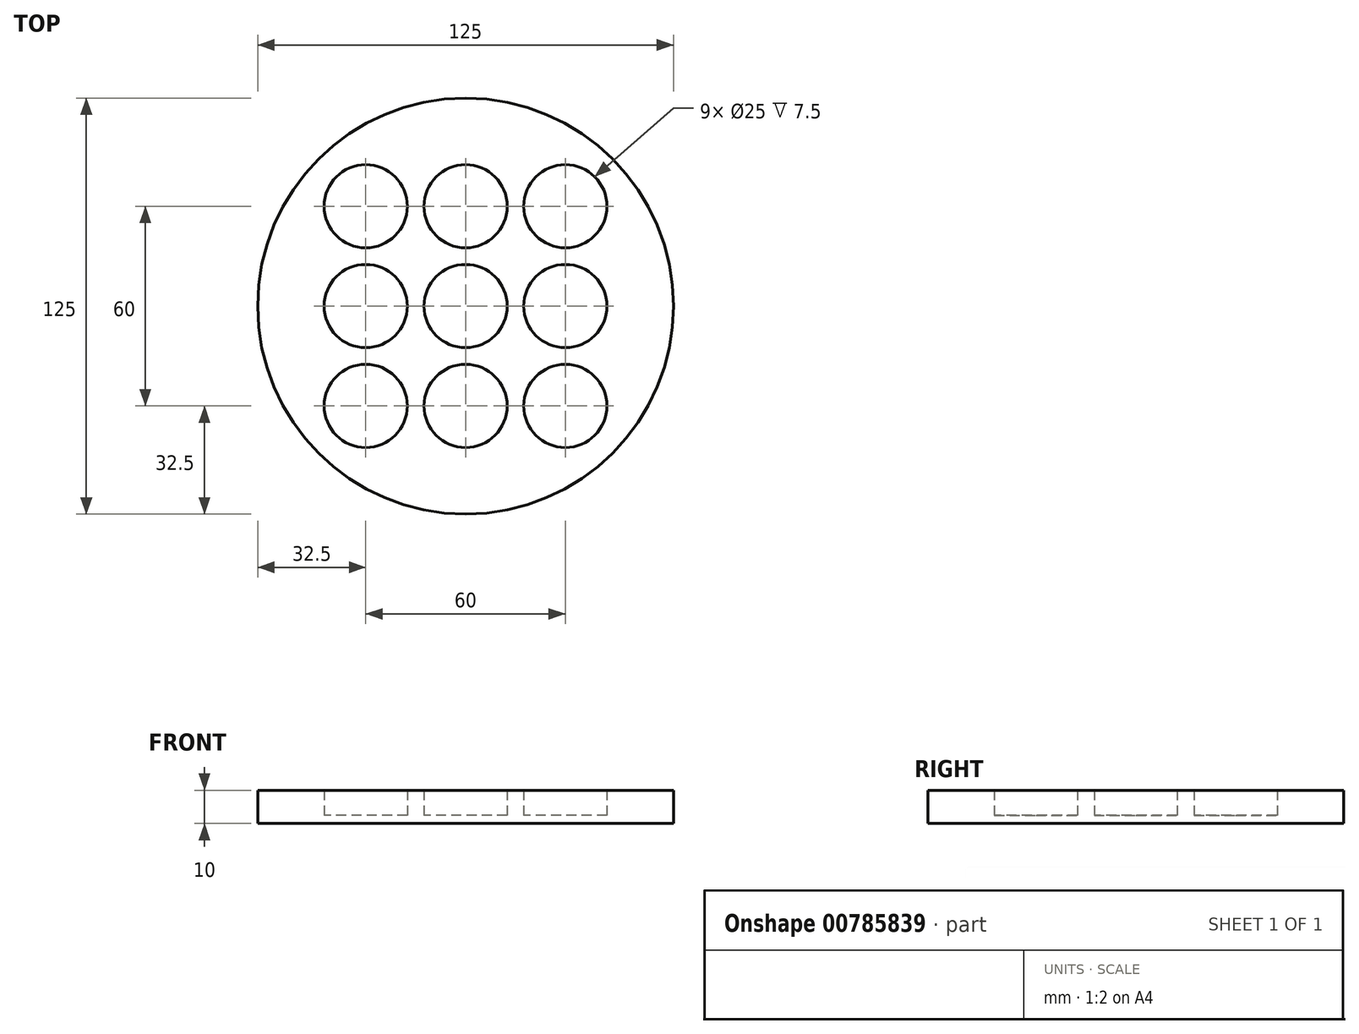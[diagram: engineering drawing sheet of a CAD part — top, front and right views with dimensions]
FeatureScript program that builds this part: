
annotation { "Feature Type Name" : "Feature", "Feature Type Description" : "" }
export const myFeature = defineFeature(function(context is Context, id is Id, definition is map)
    precondition{}
    {
        {
            var Q0;
            Q0=qCreatedBy(makeId("Top.planeOp"),FACE);
            var sketch = newSketch(context, id + "F0", { "sketchPlane" : qUnion([Q0])});
            skCircle(sketch, "E0", {"center": v(0, 0) * mm, "radius": 12.5 * mm});
            skCircle(sketch, "E1", {"center": v(0, -30) * mm, "radius": 12.5 * mm});
            skCircle(sketch, "E2", {"center": v(-30, -30) * mm, "radius": 12.5 * mm});
            skCircle(sketch, "E3", {"center": v(-30, 0) * mm, "radius": 12.5 * mm});
            skCircle(sketch, "E4", {"center": v(-30, 30) * mm, "radius": 12.5 * mm});
            skCircle(sketch, "E5", {"center": v(0, 30) * mm, "radius": 12.5 * mm});
            skCircle(sketch, "E6", {"center": v(30, 30) * mm, "radius": 12.5 * mm});
            skCircle(sketch, "E7", {"center": v(30, 0) * mm, "radius": 12.5 * mm});
            skCircle(sketch, "E8", {"center": v(30, -30) * mm, "radius": 12.5 * mm});
            skPoint(sketch, "E9.orphan", {"position": v(-62.5, 30) * mm});
            skPoint(sketch, "E10.orphan", {"position": v(0, -62.5) * mm});
            skPoint(sketch, "E11.orphan", {"position": v(-62.5, -30) * mm});
            skPoint(sketch, "E12.orphan", {"position": v(62.5, 62.5) * mm});
            skPoint(sketch, "E13.orphan", {"position": v(62.5, -62.5) * mm});
            skPoint(sketch, "E14.end.orphan", {"position": v(-62.5, -62.5) * mm});
            skPoint(sketch, "E15.0.start.orphan", {"position": v(62.5, 30) * mm});
            skPoint(sketch, "E16.orphan", {"position": v(62.5, 0) * mm});
            skPoint(sketch, "E17.0.start.orphan", {"position": v(62.5, -30) * mm});
            skCircle(sketch, "E18", {"center": v(0, 0) * mm, "radius": 62.5 * mm});
            skSolve(sketch);
        }
        {
            var Q0;
            Q0=qSketchRegion(id+"F0",true);
            extrude(context, id + "F1", {"entities" : qUnion([Q0]), "depth" : 10 * mm, "offsetDistance" : 25 * mm});
        }
        {
            var Q0;
            Q0=qCreatedBy(makeId("Top.planeOp"),FACE);
            var sketch = newSketch(context, id + "F2", { "sketchPlane" : qUnion([Q0])});
            skCircle(sketch, "E19", {"center": v(0, 0) * mm, "radius": 62.5 * mm});
            skSolve(sketch);
        }
        {
            var Q0;
            Q0=makeQuery(id+"F2.imprint","IMPRINT",FACE,{"disambiguationData":[TD([[makeQuery(id+"F2.imprint","IMPRINT",EDGE,{"derivedFrom":sQuery(id+"F2.wireOp",EDGE,"E19")}),1.0]])]});
            extrude(context, id + "F3", {"entities" : qUnion([Q0]), "operationType" : NewBodyOperationType.ADD, "depth" : 2.5 * mm, "offsetDistance" : 25 * mm});
        }
    });
